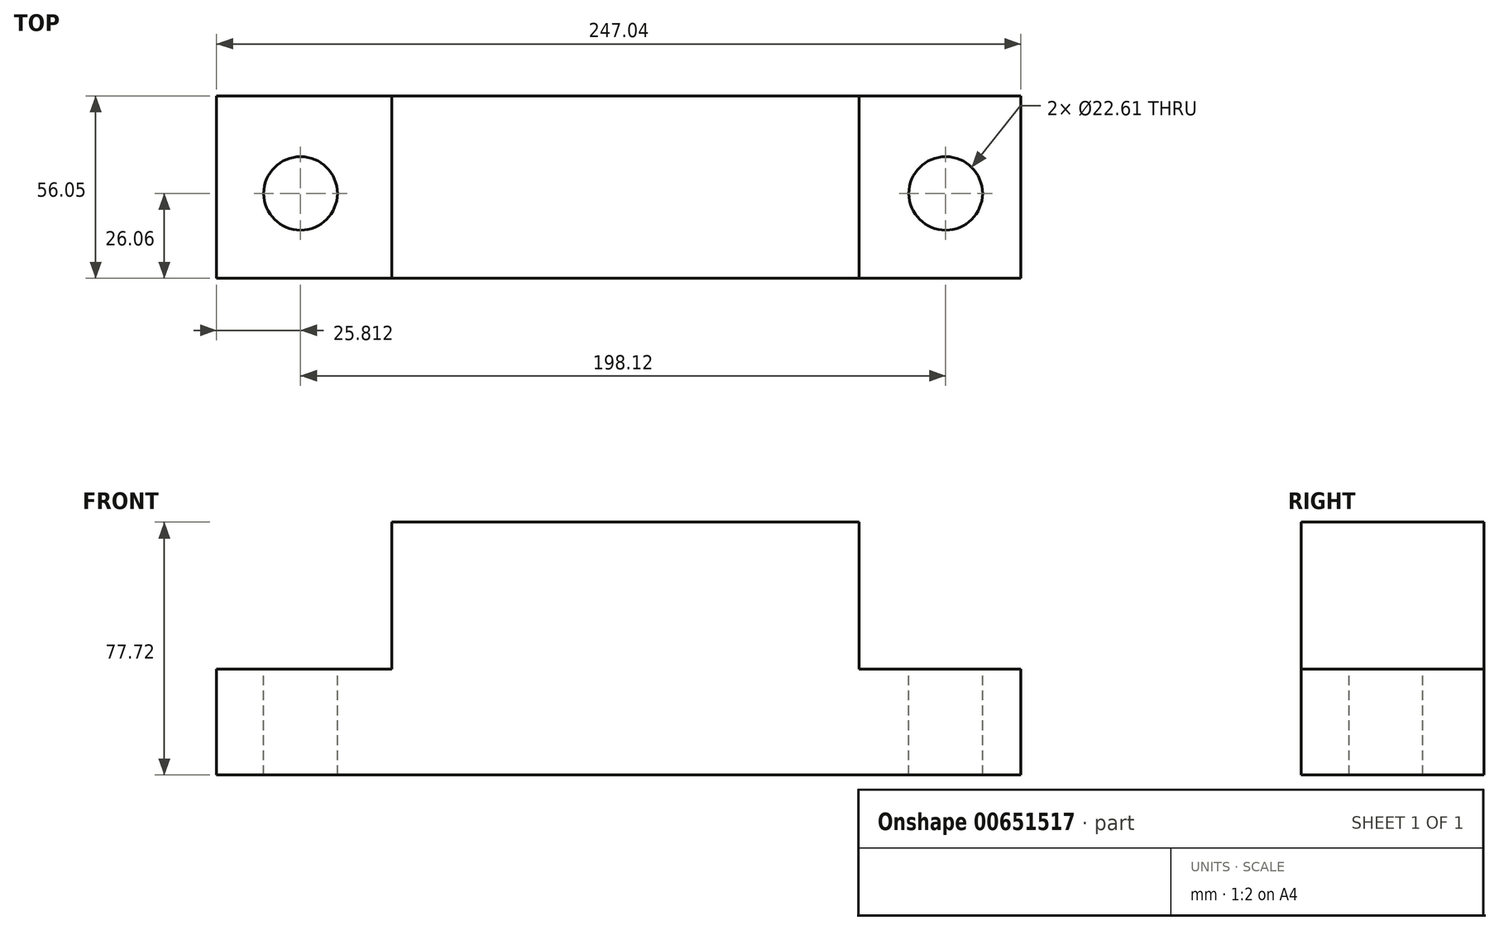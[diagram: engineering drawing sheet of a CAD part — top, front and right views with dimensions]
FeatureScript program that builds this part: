
annotation { "Feature Type Name" : "Feature", "Feature Type Description" : "" }
export const myFeature = defineFeature(function(context is Context, id is Id, definition is map)
    precondition{}
    {
        {
            var Q0;
            Q0=qCreatedBy(makeId("Top.planeOp"),FACE);
            var sketch = newSketch(context, id + "F0", { "sketchPlane" : qUnion([Q0])});
            skLineSegment(sketch, "E0.bottom", {"start": v(123.52, 29.99) * mm, "end": v(-123.52, 29.99) * mm});
            skLineSegment(sketch, "E0.top", {"start": v(123.52, -26.06) * mm, "end": v(-123.52, -26.06) * mm});
            skLineSegment(sketch, "E0.left", {"start": v(123.52, 29.99) * mm, "end": v(123.52, -26.06) * mm});
            skLineSegment(sketch, "E0.right", {"start": v(-123.52, 29.99) * mm, "end": v(-123.52, -26.06) * mm});
            skPoint(sketch, "E0.middle", {"position": v(0, 1.97) * mm});
            skSolve(sketch);
        }
        {
            var Q0;
            Q0=makeQuery(id+"F0.imprint","IMPRINT",FACE,{"disambiguationData":[TD([[makeQuery(id+"F0.imprint","IMPRINT",EDGE,{"derivedFrom":sQuery(id+"F0.wireOp",EDGE,"E0.bottom")}),1.0]])]});
            extrude(context, id + "F1", {"entities" : qUnion([Q0]), "depth" : 32.5 * mm, "offsetDistance" : 25.4 * mm});
        }
        {
            var Q0;
            Q0=makeQuery(id+"F1.opExtrude","CAP_FACE",FACE,{"disambiguationData":[OSD([sQuery(id+"F0.wireOp",EDGE,"E0.bottom"),sQuery(id+"F0.wireOp",EDGE,"E0.top"),sQuery(id+"F0.wireOp",EDGE,"E0.left"),sQuery(id+"F0.wireOp",EDGE,"E0.right")])],"isStart":false});
            var sketch = newSketch(context, id + "F2", { "sketchPlane" : qUnion([Q0])});
            skCircle(sketch, "E1", {"center": v(-97.7, 0) * mm, "radius": 11.3 * mm});
            skCircle(sketch, "E2", {"center": v(100.41, 0) * mm, "radius": 11.3 * mm});
            skSolve(sketch);
        }
        {
            var Q0;
            Q0=makeQuery(id+"F2.imprint","IMPRINT",FACE,{"disambiguationData":[TD([[makeQuery(id+"F2.imprint","IMPRINT",EDGE,{"derivedFrom":sQuery(id+"F2.wireOp",EDGE,"E2")}),1.0]])]});
            var Q1;
            Q1=makeQuery(id+"F2.imprint","IMPRINT",FACE,{"disambiguationData":[TD([[makeQuery(id+"F2.imprint","IMPRINT",EDGE,{"derivedFrom":sQuery(id+"F2.wireOp",EDGE,"E1")}),1.0]])]});
            extrude(context, id + "F3", {"entities" : qUnion([Q0, Q1]), "operationType" : NewBodyOperationType.REMOVE, "oppositeDirection" : true, "depth" : 43.43 * mm, "offsetDistance" : 25.4 * mm});
        }
        {
            var Q0;
            Q0=makeQuery(id+"F1.opExtrude","CAP_FACE",FACE,{"disambiguationData":[OSD([sQuery(id+"F0.wireOp",EDGE,"E0.bottom"),sQuery(id+"F0.wireOp",EDGE,"E0.top"),sQuery(id+"F0.wireOp",EDGE,"E0.left"),sQuery(id+"F0.wireOp",EDGE,"E0.right")])],"isStart":false});
            var sketch = newSketch(context, id + "F4", { "sketchPlane" : qUnion([Q0])});
            skLineSegment(sketch, "E3.bottom", {"start": v(-69.69, 29.99) * mm, "end": v(73.86, 29.99) * mm});
            skLineSegment(sketch, "E3.top", {"start": v(-69.69, -26.06) * mm, "end": v(73.86, -26.06) * mm});
            skLineSegment(sketch, "E3.left", {"start": v(-69.69, 29.99) * mm, "end": v(-69.69, -26.06) * mm});
            skLineSegment(sketch, "E3.right", {"start": v(73.86, 29.99) * mm, "end": v(73.86, -26.06) * mm});
            skSolve(sketch);
        }
        {
            var Q0;
            Q0=makeQuery(id+"F4.imprint","IMPRINT",FACE,{"disambiguationData":[TD([[makeQuery(id+"F4.imprint","IMPRINT",EDGE,{"derivedFrom":sQuery(id+"F4.wireOp",EDGE,"E3.bottom")}),1.0]])]});
            extrude(context, id + "F5", {"entities" : qUnion([Q0]), "operationType" : NewBodyOperationType.ADD, "depth" : 45.2 * mm, "offsetDistance" : 25.4 * mm});
        }
    });
